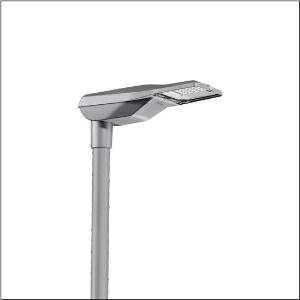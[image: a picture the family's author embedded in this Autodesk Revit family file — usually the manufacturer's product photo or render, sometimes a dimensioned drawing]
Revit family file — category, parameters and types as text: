
# Revit family: streetlight_sl_21_iq_micro___st1_0ab_5xe1m31d08db_7599
name_source: partatom
category: Lighting Fixtures
units: mm (PartAtom-declared; Revit-internal decimal feet)

## family parameters
Cut with Voids When Loaded = No
Host = Face
Light Source = No
Part Type = Normal
Room Calculation Point = No
Round Connector Dimension = Use Diameter
Shared = No

## types (1)
- --- (1 x LED, 4240 lm, 36.4 W, 3000K)
    Apparent Load = 36 VA
    CIE Flux Codes = 38 73 97 100 100
    Color Rendering = 70
    Color Temperature = 3000K
    Default Elevation = 1800 mm
    Description = Streetlight SL 21 iQ micro, mast luminaire, primary light control with lens, of PMMA, primary optical cover: cover, of toughened safety glass, transparent, light distribution: ST1.0aB, light emission: direct distribution, primary light characteristic: asymmetric, installation type: post-top, side-entry, LED, High Power LED, rated luminous flux: 4.240lm, luminous efficacy: 117lm/W, light colour: 730, colour temperature: 3000K, control gear: iQ-Comfort, control: Auto-Match, Temp-Guard, Lumen-Switch, Night-Set, Smart-Wire, Light-Fading, Desk-Remote (wireless, voltage-free reading and setting of iQ features in the workshop via application-optimized NFC function/RFID function), optimised constant luminous flux control (CLO 2.0), pre-setting: linear dimming characteristic, mains connection: 220..240V, AC, 50/60Hz, start of lifetime: 36W, end of service life: 38W, reduction: 16W, luminaire housing, of diecast aluminium, powder-coated, Siteco® metallic grey (DB 702S), corrosivity category C5 high according to DIN EN ISO 12944, please order mast flange separately, inclination adjustable: 0°, 5°, 10°, 15°, sealing non-destructively replaceable, multi-level sealing system, length: 528mm, width: 235mm, height: 110mm, mast flange for spigot size: 42mm (side-entry): 5XC10008XM4, 60/48mm (side-entry/post-top): 5XC10108XM2, 76/60mm (side-entry/post-top): 5XC10108XM1, protection rating (complete): IP66, insulation class (complete): insulation class II (safety insulation), certification: CE, ENEC, ENEC+, VDE, impact resistance: IK10, permissible operating ambient temperature for outdoor applications: -40..+50°C, standard-compliant lighting for roads and squares, packaging unit: 1 piece

Light Distribution: ST1.0aB
    Height = 110 mm
    Lamp = 1 x LED
    Lamp Light Flux = 4240 lm
    Lamp Power = 36.4 W
    Lamp count = 1
    Length = 528 mm
    Luminous efficacy = 116 lm/W
    Manufacturer = Siteco
    ModVariant = No
    Model = 5XE1M31D08DB
    Number of Poles = 1
    OnlyDefault = Yes
    Power Factor = 1
    Product Name = Streetlight SL 21 iQ micro | ST1.0aB
    Product group = mast luminaire | pylon top
    ProductGroupID = 6100
    Protection Class = Protection class II
    Protection Degree = IP 66
    RLX_Detail_Level = 1
    RLX_Emergency_Light_Flux = 0 lm
    RLX_Emergency_Type = 0
    RLX_Emergency_Type_DB = No
    RlxData = <blob elided: 98505 chars, md5=32607828>
    Socket = socket
    Standby Power = 0 W
    System Light Flux = 4240 lm
    System Power = 36 W
    Type Comments = factory setting: luminous flux: 100 % | dim-lin: 254 | 715 mA
    Type Image = l_1006881.jpg
    URL = http://relux.com
    VarID = @adj_157365
    Voltage = 0 V
    Weight = 0.00 kg
    Width = 235 mm

## geometry (parser evidence)
native form markers: Blend x4, Sweep x11
no freeform markers — native parametric forms only
